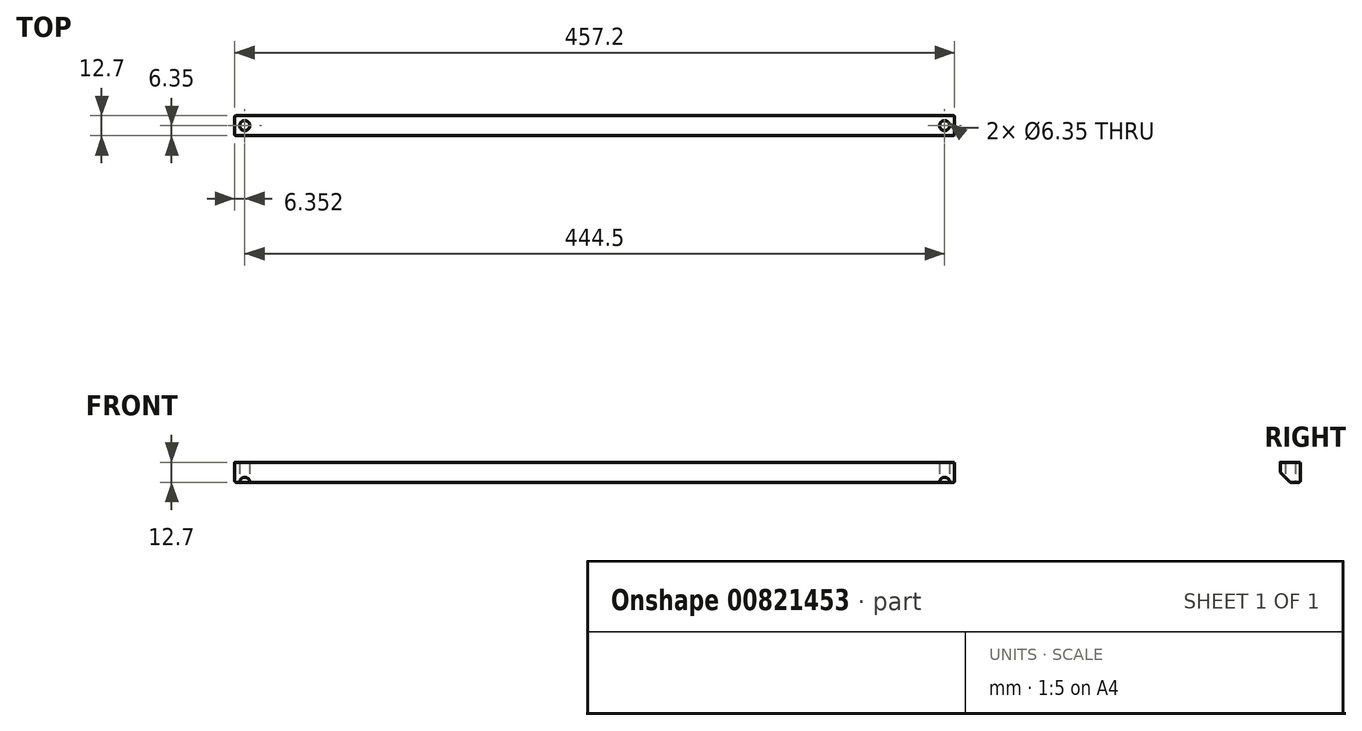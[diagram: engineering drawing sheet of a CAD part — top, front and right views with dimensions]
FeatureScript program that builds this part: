
annotation { "Feature Type Name" : "Feature", "Feature Type Description" : "" }
export const myFeature = defineFeature(function(context is Context, id is Id, definition is map)
    precondition{}
    {
        {
            var Q0;
            Q0=qCreatedBy(makeId("Top.planeOp"),FACE);
            var sketch = newSketch(context, id + "F0", { "sketchPlane" : qUnion([Q0])});
            skLineSegment(sketch, "E0.bottom", {"start": v(-224.2, -6.35) * mm, "end": v(233, -6.35) * mm});
            skLineSegment(sketch, "E0.top", {"start": v(-224.2, 6.35) * mm, "end": v(233, 6.35) * mm});
            skLineSegment(sketch, "E0.left", {"start": v(-224.2, -6.35) * mm, "end": v(-224.2, 6.35) * mm});
            skLineSegment(sketch, "E0.right", {"start": v(233, -6.35) * mm, "end": v(233, 6.35) * mm});
            skPoint(sketch, "E0.middle", {"position": v(4.4, 0) * mm});
            skCircle(sketch, "E1", {"center": v(-217.86, 0) * mm, "radius": 3.18 * mm});
            skCircle(sketch, "E2", {"center": v(226.64, 0) * mm, "radius": 3.18 * mm});
            skSolve(sketch);
        }
        {
            var Q0;
            Q0=makeQuery(id+"F0.imprint","IMPRINT",FACE,{"disambiguationData":[TD([[makeQuery(id+"F0.imprint","IMPRINT",EDGE,{"derivedFrom":sQuery(id+"F0.wireOp",EDGE,"E0.bottom")}),1.0]])]});
            extrude(context, id + "F1", {"entities" : qUnion([Q0]), "endBound" : BoundingType.SYMMETRIC, "depth" : 12.7 * mm, "offsetDistance" : 25.4 * mm});
        }
        {
            var Q0;
            Q0=makeQuery(id+"F1.opExtrude","CAP_EDGE",EDGE,{"disambiguationData":[OSD([sQuery(id+"F0.wireOp",EDGE,"E0.bottom")])],"isStart":true});
            chamfer(context, id + "F2", {"entities" : qUnion([Q0]), "width" : 6.35 * mm, "tangentPropagation" : true});
        }
        {
            var Q0;
            Q0=makeQuery(id+"F2.opChamfer","BLEND_EDGE",EDGE,{"blendedFrom":[makeQuery(id+"F1.opExtrude","CAP_EDGE",EDGE,{"disambiguationData":[OSD([sQuery(id+"F0.wireOp",EDGE,"E0.bottom")])],"isStart":true}),makeQuery(id+"F1.opExtrude","SWEPT_FACE",FACE,{"disambiguationData":[OSD([sQuery(id+"F0.wireOp",EDGE,"E0.right")])]})],"blendedInto":[makeQuery(id+"F1.opExtrude","SWEPT_FACE",FACE,{"disambiguationData":[OSD([sQuery(id+"F0.wireOp",EDGE,"E0.right")])]})]});
            var Q1;
            Q1=makeQuery(id+"F1.opExtrude","SWEPT_EDGE",EDGE,{"disambiguationData":[OSD([sQuery(id+"F0.wireOp",EDGE,"E0.bottom"),sQuery(id+"F0.wireOp",EDGE,"E0.right")])]});
            var Q2;
            Q2=makeQuery(id+"F1.opExtrude","CAP_EDGE",EDGE,{"disambiguationData":[OSD([sQuery(id+"F0.wireOp",EDGE,"E0.right")])],"isStart":true});
            var Q3;
            Q3=makeQuery(id+"F1.opExtrude","SWEPT_EDGE",EDGE,{"disambiguationData":[OSD([sQuery(id+"F0.wireOp",EDGE,"E0.top"),sQuery(id+"F0.wireOp",EDGE,"E0.right")])]});
            var Q4;
            Q4=makeQuery(id+"F2.opChamfer","BLEND_EDGE",EDGE,{"blendedFrom":[makeQuery(id+"F1.opExtrude","CAP_EDGE",EDGE,{"disambiguationData":[OSD([sQuery(id+"F0.wireOp",EDGE,"E0.bottom")])],"isStart":true}),makeQuery(id+"F1.opExtrude","SWEPT_FACE",FACE,{"disambiguationData":[OSD([sQuery(id+"F0.wireOp",EDGE,"E0.left")])]})],"blendedInto":[makeQuery(id+"F1.opExtrude","SWEPT_FACE",FACE,{"disambiguationData":[OSD([sQuery(id+"F0.wireOp",EDGE,"E0.left")])]})]});
            var Q5;
            Q5=makeQuery(id+"F1.opExtrude","SWEPT_EDGE",EDGE,{"disambiguationData":[OSD([sQuery(id+"F0.wireOp",EDGE,"E0.bottom"),sQuery(id+"F0.wireOp",EDGE,"E0.left")])]});
            var Q6;
            Q6=makeQuery(id+"F1.opExtrude","CAP_EDGE",EDGE,{"disambiguationData":[OSD([sQuery(id+"F0.wireOp",EDGE,"E0.left")])],"isStart":true});
            var Q7;
            Q7=makeQuery(id+"F1.opExtrude","SWEPT_EDGE",EDGE,{"disambiguationData":[OSD([sQuery(id+"F0.wireOp",EDGE,"E0.top"),sQuery(id+"F0.wireOp",EDGE,"E0.left")])]});
            var Q8;
            {var subQ0=sQuery(id+"F0.wireOp",EDGE,"E0.bottom");Q8=makeQuery(id+"F2.opChamfer","BLEND_EDGE",EDGE,{"blendedFrom":[makeQuery(id+"F1.opExtrude","CAP_EDGE",EDGE,{"disambiguationData":[OSD([subQ0])],"isStart":true}),makeQuery(id+"F1.opExtrude","SWEPT_FACE",FACE,{"disambiguationData":[OSD([subQ0])]})],"blendedInto":[makeQuery(id+"F1.opExtrude","SWEPT_FACE",FACE,{"disambiguationData":[OSD([subQ0])]})]});}
            var Q9;
            {var subQ0=sQuery(id+"F0.wireOp",EDGE,"E0.bottom");Q9=makeQuery(id+"F2.opChamfer","BLEND_EDGE",EDGE,{"disambiguationData":[OD(2.0)],"blendedFrom":[makeQuery(id+"F1.opExtrude","CAP_EDGE",EDGE,{"disambiguationData":[OSD([subQ0])],"isStart":true}),makeQuery(id+"F1.opExtrude","CAP_FACE",FACE,{"disambiguationData":[OSD([subQ0,sQuery(id+"F0.wireOp",EDGE,"E0.top"),sQuery(id+"F0.wireOp",EDGE,"E0.left"),sQuery(id+"F0.wireOp",EDGE,"E0.right"),sQuery(id+"F0.wireOp",EDGE,"E1"),sQuery(id+"F0.wireOp",EDGE,"E2")])],"isStart":true})],"blendedInto":[makeQuery(id+"F1.opExtrude","CAP_FACE",FACE,{"disambiguationData":[OSD([subQ0,sQuery(id+"F0.wireOp",EDGE,"E0.top"),sQuery(id+"F0.wireOp",EDGE,"E0.left"),sQuery(id+"F0.wireOp",EDGE,"E0.right"),sQuery(id+"F0.wireOp",EDGE,"E1"),sQuery(id+"F0.wireOp",EDGE,"E2")])],"isStart":true})]});}
            var Q10;
            {var subQ0=sQuery(id+"F0.wireOp",EDGE,"E0.bottom");Q10=makeQuery(id+"F2.opChamfer","BLEND_EDGE",EDGE,{"disambiguationData":[OD(0.0)],"blendedFrom":[makeQuery(id+"F1.opExtrude","CAP_EDGE",EDGE,{"disambiguationData":[OSD([subQ0])],"isStart":true}),makeQuery(id+"F1.opExtrude","CAP_FACE",FACE,{"disambiguationData":[OSD([subQ0,sQuery(id+"F0.wireOp",EDGE,"E0.top"),sQuery(id+"F0.wireOp",EDGE,"E0.left"),sQuery(id+"F0.wireOp",EDGE,"E0.right"),sQuery(id+"F0.wireOp",EDGE,"E1"),sQuery(id+"F0.wireOp",EDGE,"E2")])],"isStart":true})],"blendedInto":[makeQuery(id+"F1.opExtrude","CAP_FACE",FACE,{"disambiguationData":[OSD([subQ0,sQuery(id+"F0.wireOp",EDGE,"E0.top"),sQuery(id+"F0.wireOp",EDGE,"E0.left"),sQuery(id+"F0.wireOp",EDGE,"E0.right"),sQuery(id+"F0.wireOp",EDGE,"E1"),sQuery(id+"F0.wireOp",EDGE,"E2")])],"isStart":true})]});}
            var Q11;
            {var subQ0=sQuery(id+"F0.wireOp",EDGE,"E0.bottom");Q11=makeQuery(id+"F2.opChamfer","BLEND_EDGE",EDGE,{"disambiguationData":[OD(1.0)],"blendedFrom":[makeQuery(id+"F1.opExtrude","CAP_EDGE",EDGE,{"disambiguationData":[OSD([subQ0])],"isStart":true}),makeQuery(id+"F1.opExtrude","CAP_FACE",FACE,{"disambiguationData":[OSD([subQ0,sQuery(id+"F0.wireOp",EDGE,"E0.top"),sQuery(id+"F0.wireOp",EDGE,"E0.left"),sQuery(id+"F0.wireOp",EDGE,"E0.right"),sQuery(id+"F0.wireOp",EDGE,"E1"),sQuery(id+"F0.wireOp",EDGE,"E2")])],"isStart":true})],"blendedInto":[makeQuery(id+"F1.opExtrude","CAP_FACE",FACE,{"disambiguationData":[OSD([subQ0,sQuery(id+"F0.wireOp",EDGE,"E0.top"),sQuery(id+"F0.wireOp",EDGE,"E0.left"),sQuery(id+"F0.wireOp",EDGE,"E0.right"),sQuery(id+"F0.wireOp",EDGE,"E1"),sQuery(id+"F0.wireOp",EDGE,"E2")])],"isStart":true})]});}
            var Q12;
            Q12=makeQuery(id+"F1.opExtrude","CAP_EDGE",EDGE,{"disambiguationData":[OSD([sQuery(id+"F0.wireOp",EDGE,"E0.top")])],"isStart":true});
            fillet(context, id + "F3", {"entities" : qUnion([Q0, Q1, Q2, Q3, Q4, Q5, Q6, Q7, Q8, Q9, Q10, Q11, Q12]), "radius" : 0.8 * mm, "tangentPropagation" : true, "allowEdgeOverflow" : false});
        }
    });
